# Revit family: Прямой узел Sanext для нижнего подключения радиатора
name_source: partatom
category: Соединительные детали трубопроводов
revit_build: Autodesk Revit 2017 (Build: 20160225_1515(x64)
units: mm (PartAtom-declared; Revit-internal decimal feet)

## family parameters
Всегда вертикально = Да
На основе рабочей плоскости = Нет
Общий = Нет
При загрузке вырезать с полостями = Нет
Размер круглого соединителя = Использовать радиус
Тип детали = Соединение

## types (1)
- Узел нижнего подключения радиатора, H-образный R 3/4 Евроконус - G 3/4 Евроконус
    ADSK_Единица измерения = шт
    ADSK_Завод-изготовитель = Sanext
    ADSK_Код изделия = 4961
    ADSK_Масса = 0
    ADSK_Наименование = Узел нижнего подключения радиатора, H-образный R 3/4 Евроконус - G 3/4 Евроконус
    DN1 = 25 мм
    R = 13 мм
    S = 36 мм
    URL = http://sanext.ru
    h = 47 мм
    Изготовитель = Sanext
    Материал фитинга = DZR латунь
    Разработчик = ООО ПРОРУБИМ
    Разработчик (телефон) = +7(495)649-85-43
    Разработчик модели (URL) = http://prorubim.com
